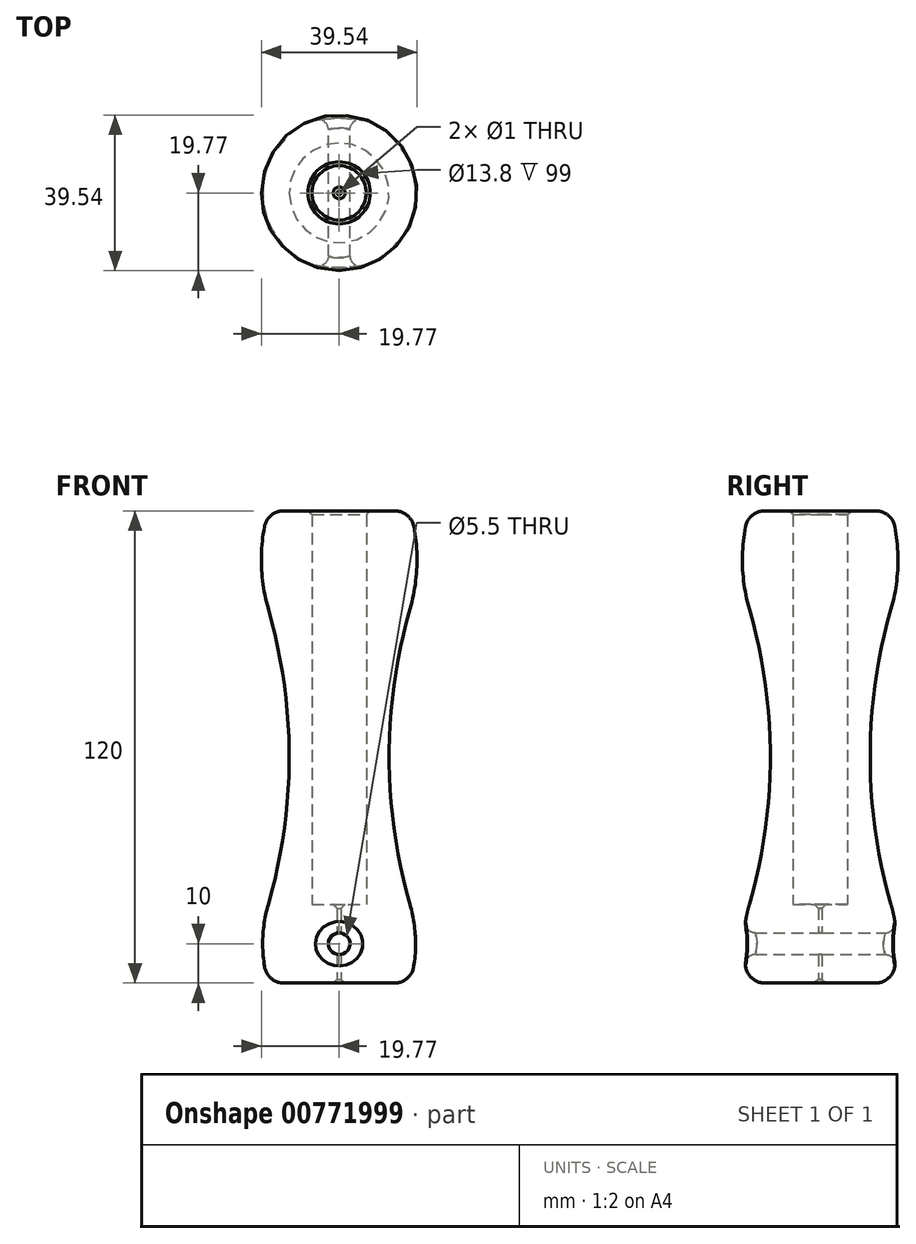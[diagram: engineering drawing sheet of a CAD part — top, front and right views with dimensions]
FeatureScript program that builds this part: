
annotation { "Feature Type Name" : "Feature", "Feature Type Description" : "" }
export const myFeature = defineFeature(function(context is Context, id is Id, definition is map)
    precondition{}
    {
        {
            var Q0;
            Q0=qCreatedBy(makeId("Front.planeOp"),FACE);
            var sketch = newSketch(context, id + "F0", { "sketchPlane" : qUnion([Q0])});
            skLineSegment(sketch, "E0", {"start": v(0, 0) * mm, "end": v(0, 124.26) * mm, "construction": true});
            skLineSegment(sketch, "E1", {"start": v(0.5, 0) * mm, "end": v(18, 0) * mm});
            skLineSegment(sketch, "E2", {"start": v(18, 0) * mm, "end": v(18, 120) * mm, "construction": true});
            skLineSegment(sketch, "E3", {"start": v(18, 120) * mm, "end": v(0, 120) * mm, "construction": true});
            skLineSegment(sketch, "E4", {"start": v(0, 95) * mm, "end": v(18, 95) * mm, "construction": true});
            skLineSegment(sketch, "E5", {"start": v(0, 20) * mm, "end": v(18, 20) * mm, "construction": true});
            skArc(sketch, "E6", {"start": v(18, 95) * mm, "mid": v(19.77, 107.5) * mm, "end": v(18, 120) * mm});
            skArc(sketch, "E7", {"start": v(18, 95) * mm, "mid": v(12.69, 57.5) * mm, "end": v(18, 20) * mm});
            skArc(sketch, "E8", {"start": v(18, 0) * mm, "mid": v(19.42, 10) * mm, "end": v(18, 20) * mm});
            skLineSegment(sketch, "E9", {"start": v(0.5, 20) * mm, "end": v(6.9, 20) * mm});
            skLineSegment(sketch, "E10", {"start": v(6.9, 20) * mm, "end": v(6.9, 120) * mm});
            skLineSegment(sketch, "E11", {"start": v(6.9, 120) * mm, "end": v(18, 120) * mm});
            skLineSegment(sketch, "E12", {"start": v(0.5, 20) * mm, "end": v(0.5, 0) * mm});
            skSolve(sketch);
        }
        {
            var Q0;
            Q0=makeQuery(id+"F0.imprint","IMPRINT",FACE,{"disambiguationData":[TD([[makeQuery(id+"F0.imprint","IMPRINT",EDGE,{"derivedFrom":sQuery(id+"F0.wireOp",EDGE,"E1")}),1.0]])]});
            var Q1;
            Q1=sQuery(id+"F0.wireOp",EDGE,"E0");
            revolve(context, id + "F1", {"surfaceOperationType" : NewSurfaceOperationType.NEW, "entities" : qUnion([Q0]), "axis" : qUnion([Q1]), "revolveType" : RevolveType.FULL});
        }
        {
            var Q0;
            Q0=makeQuery(id+"F1.opRevolve","SWEPT_EDGE",EDGE,{"disambiguationData":[OSD([sQuery(id+"F0.wireOp",EDGE,"E6"),sQuery(id+"F0.wireOp",EDGE,"E11")])]});
            var Q1;
            Q1=makeQuery(id+"F1.opRevolve","SWEPT_EDGE",EDGE,{"disambiguationData":[OSD([sQuery(id+"F0.wireOp",EDGE,"E1"),sQuery(id+"F0.wireOp",EDGE,"E8")])]});
            fillet(context, id + "F2", {"entities" : qUnion([Q0, Q1]), "radius" : 5 * mm, "tangentPropagation" : true, "allowEdgeOverflow" : false});
        }
        {
            var Q0;
            Q0=qCreatedBy(makeId("Front.planeOp"),FACE);
            var sketch = newSketch(context, id + "F3", { "sketchPlane" : qUnion([Q0])});
            skCircle(sketch, "E13", {"center": v(0, 10) * mm, "radius": 2.75 * mm});
            skSolve(sketch);
        }
        {
            var Q0;
            Q0 = qSketchRegion(id + "F3", true);
            extrude(context, id + "F4", {"entities" : qUnion([Q0]), "operationType" : NewBodyOperationType.REMOVE, "endBound" : BoundingType.SYMMETRIC, "depth" : 40 * mm, "offsetDistance" : 25 * mm});
        }
        {
            var Q0;
            Q0=makeQuery(id+"F4.boolean.opBoolean","INTERSECT",EDGE,{"disambiguationData":[OD(0.0)],"derivedFrom":[makeQuery(id+"F1.opRevolve","SWEPT_FACE",FACE,{"disambiguationData":[OSD([sQuery(id+"F0.wireOp",EDGE,"E8")])]}),makeQuery(id+"F4.opExtrude","SWEPT_FACE",FACE,{"disambiguationData":[OSD([sQuery(id+"F3.wireOp",EDGE,"E13")])]})]});
            var Q1;
            Q1=makeQuery(id+"F4.boolean.opBoolean","INTERSECT",EDGE,{"disambiguationData":[OD(1.0)],"derivedFrom":[makeQuery(id+"F1.opRevolve","SWEPT_FACE",FACE,{"disambiguationData":[OSD([sQuery(id+"F0.wireOp",EDGE,"E8")])]}),makeQuery(id+"F4.opExtrude","SWEPT_FACE",FACE,{"disambiguationData":[OSD([sQuery(id+"F3.wireOp",EDGE,"E13")])]})]});
            fillet(context, id + "F5", {"entities" : qUnion([Q0, Q1]), "radius" : 2.5 * mm, "tangentPropagation" : true, "allowEdgeOverflow" : false});
        }
        {
            var Q0;
            Q0=makeQuery(id+"F1.opRevolve","SWEPT_EDGE",EDGE,{"disambiguationData":[OSD([sQuery(id+"F0.wireOp",EDGE,"E10"),sQuery(id+"F0.wireOp",EDGE,"E11")])]});
            var Q1;
            Q1=makeQuery(id+"F1.opRevolve","SWEPT_EDGE",EDGE,{"disambiguationData":[OSD([sQuery(id+"F0.wireOp",EDGE,"E1"),sQuery(id+"F0.wireOp",EDGE,"E12")])]});
            var Q2;
            Q2=makeQuery(id+"F1.opRevolve","SWEPT_EDGE",EDGE,{"disambiguationData":[OSD([sQuery(id+"F0.wireOp",EDGE,"E9"),sQuery(id+"F0.wireOp",EDGE,"E12")])]});
            chamfer(context, id + "F6", {"entities" : qUnion([Q0, Q1, Q2]), "width" : 1 * mm, "tangentPropagation" : true});
        }
    });
